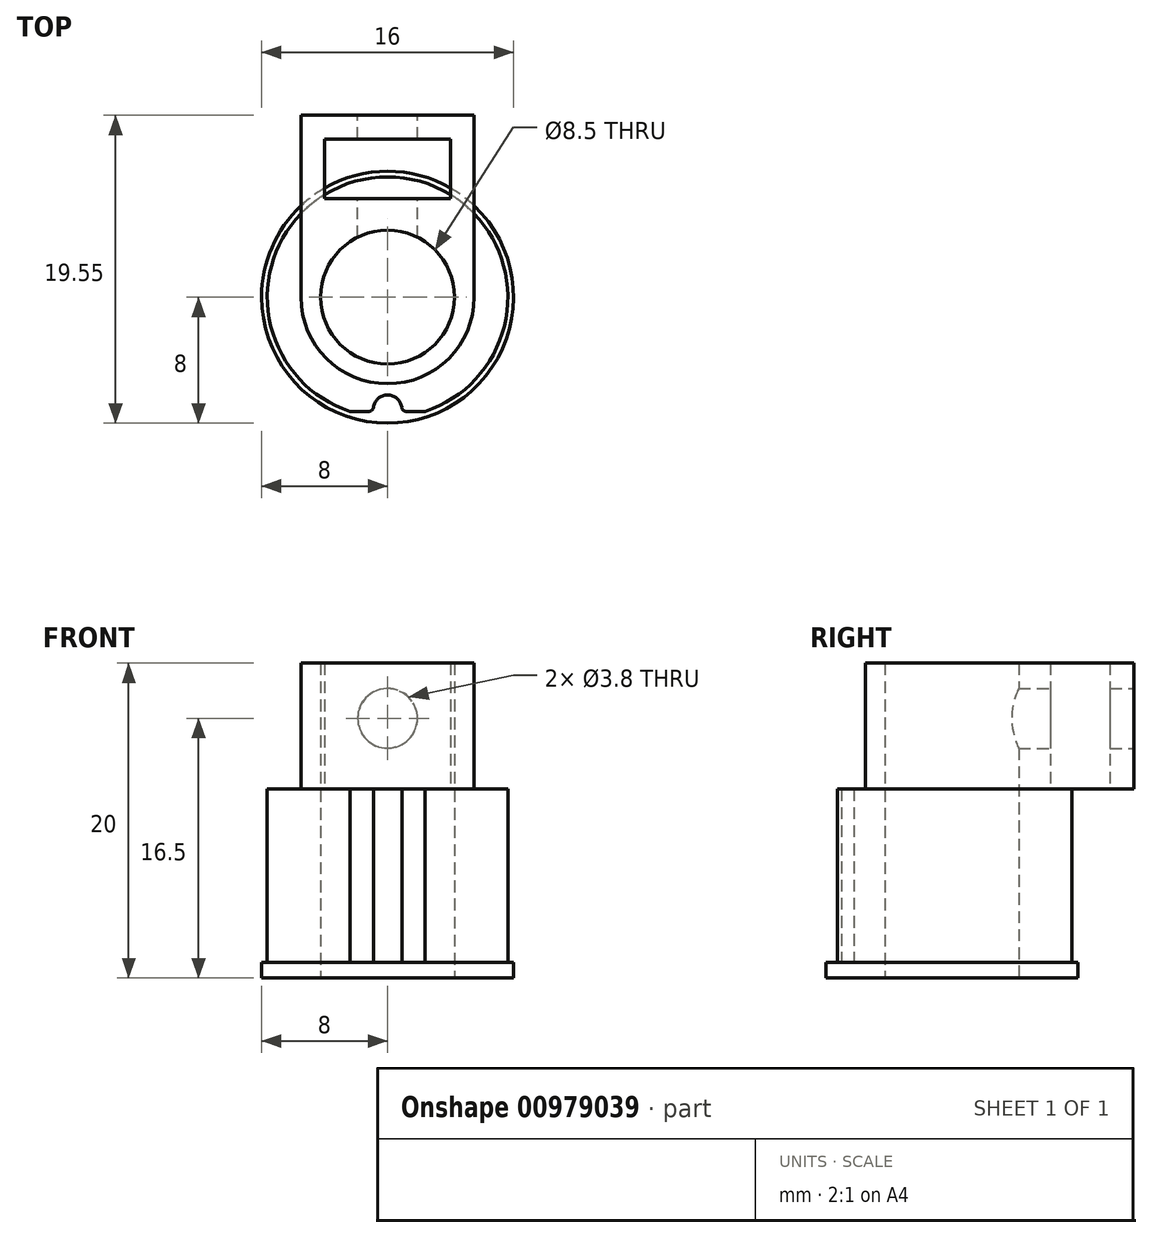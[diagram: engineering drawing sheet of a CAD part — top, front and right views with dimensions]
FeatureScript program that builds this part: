
annotation { "Feature Type Name" : "Feature", "Feature Type Description" : "" }
export const myFeature = defineFeature(function(context is Context, id is Id, definition is map)
    precondition{}
    {
        {
            var Q0;
            Q0=qCreatedBy(makeId("Top.planeOp"),FACE);
            var sketch = newSketch(context, id + "F0", { "sketchPlane" : qUnion([Q0])});
            skCircle(sketch, "E0", {"center": v(0, 0) * mm, "radius": 7.64 * mm});
            skCircle(sketch, "E1", {"center": v(0, 0) * mm, "radius": 4.25 * mm});
            skSolve(sketch);
        }
        {
            var Q0;
            Q0=makeQuery(id+"F0.imprint","IMPRINT",FACE,{"disambiguationData":[TD([[makeQuery(id+"F0.imprint","IMPRINT",EDGE,{"derivedFrom":sQuery(id+"F0.wireOp",EDGE,"E0")}),1.0]])]});
            extrude(context, id + "F1", {"entities" : qUnion([Q0]), "depth" : 11 * mm, "offsetDistance" : 25 * mm});
        }
        {
            var Q0;
            Q0=qCreatedBy(makeId("Top.planeOp"),FACE);
            var sketch = newSketch(context, id + "F2", { "sketchPlane" : qUnion([Q0])});
            skArc(sketch, "E2", {"start": v(0, -6.21) * mm, "mid": v(-0.6, -6.44) * mm, "end": v(-0.9, -7.01) * mm});
            skLineSegment(sketch, "E3", {"start": v(-0.9, -7) * mm, "end": v(-0.9, -7.01) * mm});
            skLineSegment(sketch, "E4", {"start": v(-1.19, -7.26) * mm, "end": v(-2.39, -7.26) * mm});
            skArc(sketch, "E5.filletArc", {"start": v(-1.19, -7.26) * mm, "mid": v(-1, -7.18) * mm, "end": v(-0.9, -7) * mm});
            skArc(sketch, "E6.MirrorCS", {"start": v(0, -6.21) * mm, "mid": v(0.6, -6.44) * mm, "end": v(0.9, -7.01) * mm});
            skLineSegment(sketch, "E7.MirrorCS", {"start": v(0.9, -7) * mm, "end": v(0.9, -7.01) * mm});
            skArc(sketch, "E8.MirrorCS", {"start": v(1.19, -7.26) * mm, "mid": v(1, -7.18) * mm, "end": v(0.9, -7) * mm});
            skCircle(sketch, "E9.0", {"center": v(0, 0) * mm, "radius": 7.64 * mm});
            skLineSegment(sketch, "E10.MirrorCS", {"start": v(1.19, -7.26) * mm, "end": v(2.39, -7.26) * mm});
            skSolve(sketch);
        }
        {
            var Q0;
            Q0=makeQuery(id+"F2.imprint","IMPRINT",FACE,{"disambiguationData":[TD([[makeQuery(id+"F2.imprint","IMPRINT",EDGE,{"derivedFrom":sQuery(id+"F2.wireOp",EDGE,"E2")}),1.0]])]});
            extrude(context, id + "F3", {"entities" : qUnion([Q0]), "operationType" : NewBodyOperationType.REMOVE, "endBound" : BoundingType.THROUGH_ALL, "depth" : 25 * mm, "offsetDistance" : 25 * mm});
        }
        {
            var Q0;
            Q0=makeQuery(id+"F1.opExtrude","CAP_FACE",FACE,{"disambiguationData":[OSD([sQuery(id+"F0.wireOp",EDGE,"E0"),sQuery(id+"F0.wireOp",EDGE,"E1")])],"isStart":true});
            var sketch = newSketch(context, id + "F4", { "sketchPlane" : qUnion([Q0])});
            skCircle(sketch, "E11", {"center": v(0, 0) * mm, "radius": 8 * mm});
            skCircle(sketch, "E12.0", {"center": v(0, 0) * mm, "radius": 4.25 * mm});
            skSolve(sketch);
        }
        {
            var Q0;
            Q0 = qSketchRegion(id + "F4", true);
            extrude(context, id + "F5", {"entities" : qUnion([Q0]), "operationType" : NewBodyOperationType.ADD, "depth" : 1 * mm, "offsetDistance" : 25 * mm});
        }
        {
            var Q0;
            Q0=makeQuery(id+"F1.opExtrude","CAP_FACE",FACE,{"disambiguationData":[OSD([sQuery(id+"F0.wireOp",EDGE,"E0"),sQuery(id+"F0.wireOp",EDGE,"E1")])],"isStart":false});
            var sketch = newSketch(context, id + "F6", { "sketchPlane" : qUnion([Q0])});
            skCircle(sketch, "E13.0", {"center": v(0, 0) * mm, "radius": 4.25 * mm});
            skArc(sketch, "E14", {"start": v(-5.5, 0) * mm, "mid": v(0, -5.5) * mm, "end": v(5.5, 0) * mm});
            skLineSegment(sketch, "E15.bottom", {"start": v(-4, 10.05) * mm, "end": v(4, 10.05) * mm});
            skLineSegment(sketch, "E15.top", {"start": v(-4, 6.25) * mm, "end": v(4, 6.25) * mm});
            skLineSegment(sketch, "E15.left", {"start": v(-4, 10.05) * mm, "end": v(-4, 6.25) * mm});
            skLineSegment(sketch, "E15.right", {"start": v(4, 10.05) * mm, "end": v(4, 6.25) * mm});
            skPoint(sketch, "E15.middle", {"position": v(0, 8.15) * mm});
            skPoint(sketch, "E15.middle.positionSnap0", {"position": v(0, 6.21) * mm});
            skPoint(sketch, "E15.centerSnap0", {"position": v(0, 6.21) * mm});
            skLineSegment(sketch, "E16.0", {"start": v(5.5, 11.55) * mm, "end": v(5.5, 0) * mm});
            skLineSegment(sketch, "E16.1", {"start": v(-5.5, 11.55) * mm, "end": v(5.5, 11.55) * mm});
            skLineSegment(sketch, "E16.2", {"start": v(-5.5, 11.55) * mm, "end": v(-5.5, 0) * mm});
            skSolve(sketch);
        }
        {
            var Q0;
            Q0=makeQuery(id+"F6.imprint","IMPRINT",FACE,{"disambiguationData":[TD([[makeQuery(id+"F6.imprint","IMPRINT",EDGE,{"derivedFrom":sQuery(id+"F6.wireOp",EDGE,"E13.0")}),-1.0]])]});
            var Q1;
            {var subQ43=sQuery(id+"F6.wireOp",EDGE,"E16.1");Q1=makeQuery(id+"F6.imprint","IMPRINT",FACE,{"disambiguationData":[TD([[makeQuery(id+"F6.imprint","IMPRINT",EDGE,{"derivedFrom":subQ43}),-1.0]])]});}
            var Q2;
            {var subQ0=sQuery(id+"F6.wireOp",EDGE,"81TP7Dqw-c89s-Vf9j-myAQ-n5WEl5U3WT9n");Q2=makeQuery(id+"F6.imprint","IMPRINT",FACE,{"disambiguationData":[TD([[makeQuery(id+"F6.imprint","IMPRINT",EDGE,{"derivedFrom":subQ0}),1.0]])]});}
            var Q3;
            {var subQ0=sQuery(id+"F6.wireOp",EDGE,"SeUKUaWj-CXGH-NK2I-CF5v-RfjhXchw411U");Q3=makeQuery(id+"F6.imprint","IMPRINT",FACE,{"disambiguationData":[TD([[makeQuery(id+"F6.imprint","IMPRINT",EDGE,{"derivedFrom":subQ0}),-1.0]])]});}
            var Q4;
            {var subQ0=sQuery(id+"F6.wireOp",EDGE,"E15.bottom");var subQ1=sQuery(id+"F2.wireOp",EDGE,"E5.filletArc");var subQ2=makeQuery(id+"FAlBmtbSBvSvOUU_1.8.F3.opExtrude","SWEPT_FACE",FACE,{"disambiguationData":[OSD([subQ1])]});var subQ3=sQuery(id+"F0.wireOp",EDGE,"E0");var subQ4=makeQuery(id+"F1.opExtrude","CAP_FACE",FACE,{"disambiguationData":[OSD([subQ3,sQuery(id+"F0.wireOp",EDGE,"E1")])],"isStart":false});var subQ5=subQ4;var subQ6=makeQuery(id+"FAlBmtbSBvSvOUU_1.8.F3.boolean.opBoolean","INTERSECT",EDGE,{"derivedFrom":[subQ5,subQ2]});var subQ7=makeQuery(id+"F6.imprint","INTERSECT",VERTEX,{"derivedFrom":[subQ6,subQ0]});Q4=makeQuery(id+"F6.imprint","IMPRINT",FACE,{"disambiguationData":[TD([[makeQuery(id+"F6.imprint","IMPRINT",EDGE,{"disambiguationData":[TD([[subQ7,-1.0]])],"derivedFrom":subQ0}),1.0]])]});}
            var Q5;
            {var subQ0=sQuery(id+"F6.wireOp",EDGE,"E15.bottom");var subQ1=sQuery(id+"F2.wireOp",EDGE,"E5.filletArc");var subQ2=makeQuery(id+"FAlBmtbSBvSvOUU_1.9.F3.opExtrude","SWEPT_FACE",FACE,{"disambiguationData":[OSD([subQ1])]});var subQ3=sQuery(id+"F0.wireOp",EDGE,"E0");var subQ4=makeQuery(id+"F1.opExtrude","CAP_FACE",FACE,{"disambiguationData":[OSD([subQ3,sQuery(id+"F0.wireOp",EDGE,"E1")])],"isStart":false});var subQ5=subQ4;var subQ6=makeQuery(id+"FAlBmtbSBvSvOUU_1.9.F3.boolean.opBoolean","INTERSECT",EDGE,{"derivedFrom":[subQ5,subQ2]});var subQ7=makeQuery(id+"F6.imprint","INTERSECT",VERTEX,{"derivedFrom":[subQ6,subQ0]});Q5=makeQuery(id+"F6.imprint","IMPRINT",FACE,{"disambiguationData":[TD([[makeQuery(id+"F6.imprint","IMPRINT",EDGE,{"disambiguationData":[TD([[subQ7,-1.0]])],"derivedFrom":subQ0}),1.0]])]});}
            var Q6;
            {var subQ0=sQuery(id+"F6.wireOp",EDGE,"E15.top");var subQ1=makeQuery(id+"F1.opExtrude","CAP_FACE",FACE,{"disambiguationData":[OSD([sQuery(id+"F0.wireOp",EDGE,"E0"),sQuery(id+"F0.wireOp",EDGE,"E1")])],"isStart":false});var subQ4=makeQuery(id+"FAlBmtbSBvSvOUU_1.7.F3.boolean.opBoolean","INTERSECT",EDGE,{"derivedFrom":[subQ1,makeQuery(id+"FAlBmtbSBvSvOUU_1.7.F3.opExtrude","SWEPT_FACE",FACE,{"disambiguationData":[OSD([sQuery(id+"F2.wireOp",EDGE,"E5.filletArc")])]})]});var subQ5=makeQuery(id+"F6.imprint","INTERSECT",VERTEX,{"disambiguationData":[OD(0.0)],"derivedFrom":[subQ4,subQ0]});Q6=makeQuery(id+"F6.imprint","IMPRINT",FACE,{"disambiguationData":[TD([[makeQuery(id+"F6.imprint","IMPRINT",EDGE,{"disambiguationData":[TD([[subQ5,1.0]])],"derivedFrom":subQ0}),-1.0]])]});}
            var Q7;
            {var subQ0=sQuery(id+"F6.wireOp",EDGE,"E15.top");var subQ1=makeQuery(id+"F1.opExtrude","CAP_FACE",FACE,{"disambiguationData":[OSD([sQuery(id+"F0.wireOp",EDGE,"E0"),sQuery(id+"F0.wireOp",EDGE,"E1")])],"isStart":false});var subQ2=makeQuery(id+"FAlBmtbSBvSvOUU_1.9.F3.boolean.opBoolean","INTERSECT",EDGE,{"derivedFrom":[subQ1,makeQuery(id+"FAlBmtbSBvSvOUU_1.9.F3.opExtrude","SWEPT_FACE",FACE,{"disambiguationData":[OSD([sQuery(id+"F2.wireOp",EDGE,"E8.MirrorCS")])]})]});var subQ3=makeQuery(id+"F6.imprint","INTERSECT",VERTEX,{"disambiguationData":[OD(1.0)],"derivedFrom":[subQ2,subQ0]});Q7=makeQuery(id+"F6.imprint","IMPRINT",FACE,{"disambiguationData":[TD([[makeQuery(id+"F6.imprint","IMPRINT",EDGE,{"disambiguationData":[TD([[subQ3,-1.0]])],"derivedFrom":subQ0}),-1.0]])]});}
            extrude(context, id + "F7", {"entities" : qUnion([Q0, Q1, Q2, Q3, Q4, Q5, Q6, Q7]), "operationType" : NewBodyOperationType.ADD, "depth" : 8 * mm, "offsetDistance" : 25 * mm});
        }
        {
            var Q0;
            Q0=makeQuery(id+"F7.opExtrude","SWEPT_FACE",FACE,{"disambiguationData":[OSD([sQuery(id+"F6.wireOp",EDGE,"E16.1")])]});
            var sketch = newSketch(context, id + "F8", { "sketchPlane" : qUnion([Q0])});
            skCircle(sketch, "E17", {"center": v(0, 15.5) * mm, "radius": 1.9 * mm});
            skSolve(sketch);
        }
        {
            var Q0;
            Q0=makeQuery(id+"F8.imprint","IMPRINT",FACE,{"disambiguationData":[TD([[makeQuery(id+"F8.imprint","IMPRINT",EDGE,{"derivedFrom":sQuery(id+"F8.wireOp",EDGE,"E17")}),1.0]])]});
            extrude(context, id + "F9", {"entities" : qUnion([Q0]), "operationType" : NewBodyOperationType.REMOVE, "oppositeDirection" : true, "depth" : 10 * mm, "offsetDistance" : 25 * mm});
        }
    });
